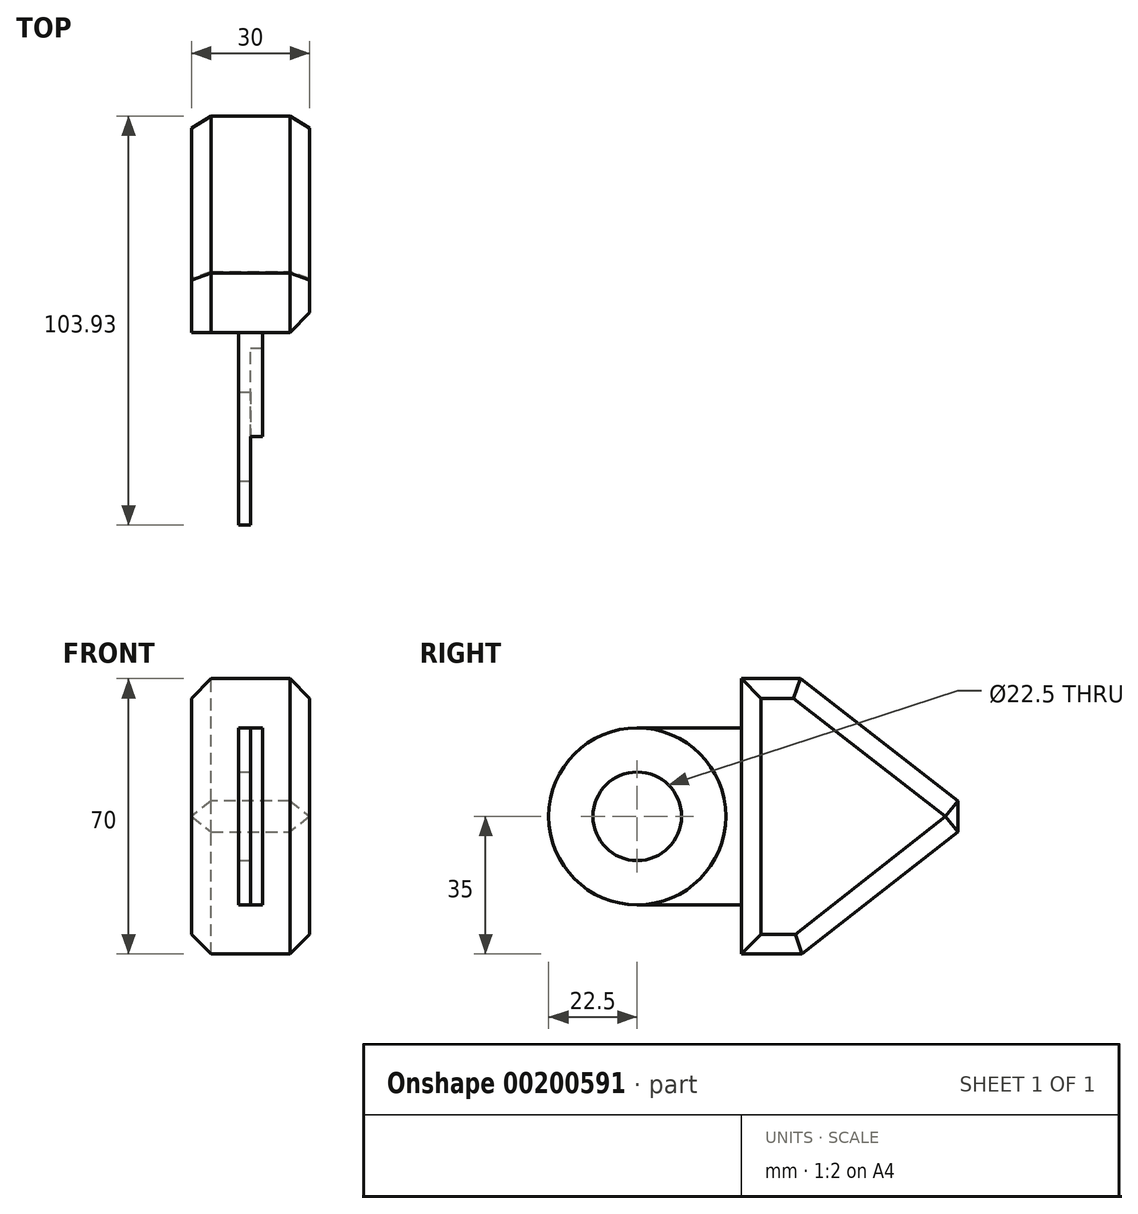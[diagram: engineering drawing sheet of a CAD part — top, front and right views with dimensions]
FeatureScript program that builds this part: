
annotation { "Feature Type Name" : "Feature", "Feature Type Description" : "" }
export const myFeature = defineFeature(function(context is Context, id is Id, definition is map)
    precondition{}
    {
        {
            var Q0;
            Q0=qCreatedBy(makeId("Right.planeOp"),FACE);
            var sketch = newSketch(context, id + "F0", { "sketchPlane" : qUnion([Q0])});
            skCircle(sketch, "E0", {"center": v(0, 0) * mm, "radius": 22.5 * mm});
            skCircle(sketch, "E1", {"center": v(0, 0) * mm, "radius": 11.25 * mm});
            skLineSegment(sketch, "E2", {"start": v(0, 0) * mm, "end": v(60.5, 0) * mm, "construction": true});
            skLineSegment(sketch, "E3.bottom", {"start": v(26.46, 35) * mm, "end": v(41.46, 35) * mm});
            skLineSegment(sketch, "E3.top", {"start": v(26.46, -35) * mm, "end": v(41.9, -35) * mm});
            skLineSegment(sketch, "E3.left", {"start": v(26.46, 35) * mm, "end": v(26.46, -35) * mm});
            skPoint(sketch, "E3.middle", {"position": v(60.5, 0) * mm});
            skLineSegment(sketch, "E4", {"start": v(41.46, 35) * mm, "end": v(86.46, 0) * mm});
            skLineSegment(sketch, "E5", {"start": v(86.46, 0) * mm, "end": v(41.9, -35) * mm});
            skPoint(sketch, "E3.right.start.orphan", {"position": v(94.54, 35) * mm});
            skPoint(sketch, "E6.orphan", {"position": v(94.54, -35) * mm});
            skLineSegment(sketch, "E7", {"start": v(0, 22.5) * mm, "end": v(26.46, 22.5) * mm});
            skLineSegment(sketch, "E8", {"start": v(0, -22.5) * mm, "end": v(26.46, -22.5) * mm});
            skSolve(sketch);
        }
        {
            var Q0;
            {var subQ3=sQuery(id+"F0.wireOp",EDGE,"E3.bottom");Q0=makeQuery(id+"F0.imprint","IMPRINT",FACE,{"disambiguationData":[TD([[makeQuery(id+"F0.imprint","IMPRINT",EDGE,{"derivedFrom":subQ3}),-1.0]])]});}
            extrude(context, id + "F1", {"entities" : qUnion([Q0]), "oppositeDirection" : true, "depth" : 15 * mm, "hasSecondDirection" : true, "secondDirectionOppositeDirection" : false, "secondDirectionDepth" : 15 * mm});
        }
        {
            var Q0;
            {var subQ0=sQuery(id+"F0.wireOp",EDGE,"E7");Q0=makeQuery(id+"F0.imprint","IMPRINT",FACE,{"disambiguationData":[TD([[makeQuery(id+"F0.imprint","IMPRINT",EDGE,{"derivedFrom":subQ0}),-1.0]])]});}
            extrude(context, id + "F2", {"entities" : qUnion([Q0]), "operationType" : NewBodyOperationType.ADD, "oppositeDirection" : true, "depth" : 3 * mm, "hasSecondDirection" : true, "secondDirectionOppositeDirection" : false, "secondDirectionDepth" : 3 * mm});
        }
        {
            var Q0;
            Q0=makeQuery(id+"F0.imprint","IMPRINT",FACE,{"disambiguationData":[TD([[makeQuery(id+"F0.imprint","IMPRINT",EDGE,{"derivedFrom":sQuery(id+"F0.wireOp",EDGE,"E1")}),-1.0]])]});
            extrude(context, id + "F3", {"entities" : qUnion([Q0]), "operationType" : NewBodyOperationType.ADD, "oppositeDirection" : true, "depth" : 3 * mm});
        }
        {
            var Q0;
            Q0=makeQuery(id+"F1.opExtrude","CAP_EDGE",EDGE,{"disambiguationData":[OSD([sQuery(id+"F0.wireOp",EDGE,"E4")])],"isStart":true});
            var Q1;
            Q1=makeQuery(id+"F1.opExtrude","CAP_EDGE",EDGE,{"disambiguationData":[OSD([sQuery(id+"F0.wireOp",EDGE,"E3.bottom")])],"isStart":true});
            var Q2;
            Q2=makeQuery(id+"F1.opExtrude","CAP_EDGE",EDGE,{"disambiguationData":[OSD([sQuery(id+"F0.wireOp",EDGE,"E3.left")])],"isStart":true});
            var Q3;
            Q3=makeQuery(id+"F1.opExtrude","CAP_EDGE",EDGE,{"disambiguationData":[OSD([sQuery(id+"F0.wireOp",EDGE,"E3.top")])],"isStart":true});
            var Q4;
            Q4=makeQuery(id+"F1.opExtrude","CAP_EDGE",EDGE,{"disambiguationData":[OSD([sQuery(id+"F0.wireOp",EDGE,"E5")])],"isStart":true});
            var Q5;
            Q5=makeQuery(id+"F1.opExtrude","SWEPT_EDGE",EDGE,{"disambiguationData":[OSD([sQuery(id+"F0.wireOp",EDGE,"E4"),sQuery(id+"F0.wireOp",EDGE,"E5")])]});
            var Q6;
            Q6=makeQuery(id+"F1.opExtrude","CAP_EDGE",EDGE,{"disambiguationData":[OSD([sQuery(id+"F0.wireOp",EDGE,"E4")])],"isStart":false});
            var Q7;
            Q7=makeQuery(id+"F1.opExtrude","CAP_EDGE",EDGE,{"disambiguationData":[OSD([sQuery(id+"F0.wireOp",EDGE,"E3.bottom")])],"isStart":false});
            var Q8;
            Q8=makeQuery(id+"F1.opExtrude","CAP_EDGE",EDGE,{"disambiguationData":[OSD([sQuery(id+"F0.wireOp",EDGE,"E5")])],"isStart":false});
            var Q9;
            Q9=makeQuery(id+"F1.opExtrude","CAP_EDGE",EDGE,{"disambiguationData":[OSD([sQuery(id+"F0.wireOp",EDGE,"E3.top")])],"isStart":false});
            chamfer(context, id + "F4", {"entities" : qUnion([Q0, Q1, Q2, Q3, Q4, Q5, Q6, Q7, Q8, Q9]), "width" : 5 * mm, "tangentPropagation" : true});
        }
    });
